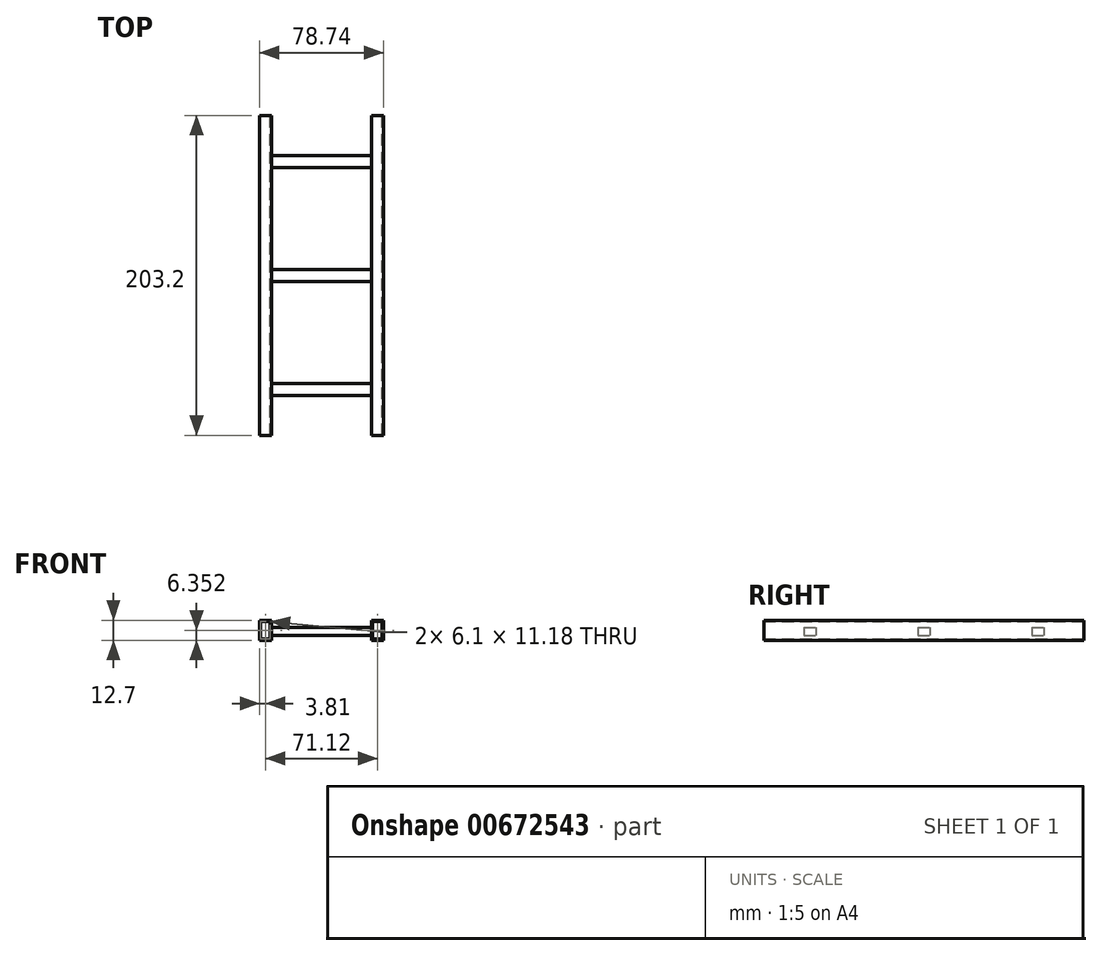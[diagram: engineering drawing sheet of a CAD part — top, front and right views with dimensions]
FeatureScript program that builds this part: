
annotation { "Feature Type Name" : "Feature", "Feature Type Description" : "" }
export const myFeature = defineFeature(function(context is Context, id is Id, definition is map)
    precondition{}
    {
        {
            var Q0;
            Q0=qCreatedBy(makeId("Front.planeOp"),FACE);
            var sketch = newSketch(context, id + "F0", { "sketchPlane" : qUnion([Q0])});
            skLineSegment(sketch, "E0.bottom", {"start": v(-39.37, 0.36) * mm, "end": v(-31.75, 0.36) * mm});
            skLineSegment(sketch, "E0.top", {"start": v(-39.37, -12.34) * mm, "end": v(-31.75, -12.34) * mm});
            skLineSegment(sketch, "E0.left", {"start": v(-39.37, 0.36) * mm, "end": v(-39.37, -12.34) * mm});
            skLineSegment(sketch, "E0.right", {"start": v(-31.75, 0.36) * mm, "end": v(-31.75, -12.34) * mm});
            skLineSegment(sketch, "E1.MirrorCS", {"start": v(31.75, 0.36) * mm, "end": v(31.75, -12.34) * mm});
            skLineSegment(sketch, "E2.MirrorCS", {"start": v(39.37, 0.36) * mm, "end": v(31.75, 0.36) * mm});
            skLineSegment(sketch, "E3.MirrorCS", {"start": v(39.37, 0.36) * mm, "end": v(39.37, -12.34) * mm});
            skLineSegment(sketch, "E4.MirrorCS", {"start": v(39.37, -12.34) * mm, "end": v(31.75, -12.34) * mm});
            skLineSegment(sketch, "E5.bottom", {"start": v(-38.6, -0.4) * mm, "end": v(-32.51, -0.4) * mm});
            skLineSegment(sketch, "E5.top", {"start": v(-38.6, -11.58) * mm, "end": v(-32.51, -11.58) * mm});
            skLineSegment(sketch, "E5.left", {"start": v(-38.6, -0.4) * mm, "end": v(-38.6, -11.58) * mm});
            skLineSegment(sketch, "E5.right", {"start": v(-32.51, -0.4) * mm, "end": v(-32.51, -11.58) * mm});
            skLineSegment(sketch, "E6.MirrorCS", {"start": v(38.6, -0.4) * mm, "end": v(32.51, -0.4) * mm});
            skLineSegment(sketch, "E7.MirrorCS", {"start": v(38.6, -0.4) * mm, "end": v(38.6, -11.58) * mm});
            skLineSegment(sketch, "E8.MirrorCS", {"start": v(38.6, -11.58) * mm, "end": v(32.51, -11.58) * mm});
            skLineSegment(sketch, "E9.MirrorCS", {"start": v(32.51, -0.4) * mm, "end": v(32.51, -11.58) * mm});
            skSolve(sketch);
        }
        {
            var Q0;
            Q0=makeQuery(id+"F0.imprint","IMPRINT",FACE,{"disambiguationData":[TD([[makeQuery(id+"F0.imprint","IMPRINT",EDGE,{"derivedFrom":sQuery(id+"F0.wireOp",EDGE,"E0.bottom")}),-1.0]])]});
            var Q1;
            Q1=makeQuery(id+"F0.imprint","IMPRINT",FACE,{"disambiguationData":[TD([[makeQuery(id+"F0.imprint","IMPRINT",EDGE,{"derivedFrom":sQuery(id+"F0.wireOp",EDGE,"E1.MirrorCS")}),1.0]])]});
            extrude(context, id + "F1", {"entities" : qUnion([Q0, Q1]), "endBound" : BoundingType.SYMMETRIC, "depth" : 203.2 * mm, "offsetDistance" : 25.4 * mm});
        }
        {
            var Q0;
            Q0=makeQuery(id+"F1.opExtrude","SWEPT_FACE",FACE,{"disambiguationData":[OSD([sQuery(id+"F0.wireOp",EDGE,"E0.right")])]});
            var sketch = newSketch(context, id + "F2", { "sketchPlane" : qUnion([Q0])});
            skLineSegment(sketch, "E10.bottom", {"start": v(-76.2, -4.28) * mm, "end": v(-68.58, -4.28) * mm});
            skLineSegment(sketch, "E10.top", {"start": v(-76.2, -9.36) * mm, "end": v(-68.58, -9.36) * mm});
            skLineSegment(sketch, "E10.left", {"start": v(-76.2, -4.28) * mm, "end": v(-76.2, -9.36) * mm});
            skLineSegment(sketch, "E10.right", {"start": v(-68.58, -4.28) * mm, "end": v(-68.58, -9.36) * mm});
            skLineSegment(sketch, "E11.bottom", {"start": v(-3.8, -4.28) * mm, "end": v(3.81, -4.28) * mm});
            skLineSegment(sketch, "E11.top", {"start": v(-3.8, -9.36) * mm, "end": v(3.81, -9.36) * mm});
            skLineSegment(sketch, "E11.left", {"start": v(-3.8, -4.28) * mm, "end": v(-3.8, -9.36) * mm});
            skLineSegment(sketch, "E11.right", {"start": v(3.81, -4.28) * mm, "end": v(3.81, -9.36) * mm});
            skLineSegment(sketch, "E12.bottom", {"start": v(68.58, -4.28) * mm, "end": v(76.2, -4.28) * mm});
            skLineSegment(sketch, "E12.top", {"start": v(68.58, -9.36) * mm, "end": v(76.2, -9.36) * mm});
            skLineSegment(sketch, "E12.left", {"start": v(68.58, -4.28) * mm, "end": v(68.58, -9.36) * mm});
            skLineSegment(sketch, "E12.right", {"start": v(76.2, -4.28) * mm, "end": v(76.2, -9.36) * mm});
            skSolve(sketch);
        }
        {
            var Q0;
            Q0=makeQuery(id+"F2.imprint","IMPRINT",FACE,{"disambiguationData":[TD([[makeQuery(id+"F2.imprint","IMPRINT",EDGE,{"derivedFrom":sQuery(id+"F2.wireOp",EDGE,"E10.bottom")}),-1.0]])]});
            var Q1;
            Q1=makeQuery(id+"F2.imprint","IMPRINT",FACE,{"disambiguationData":[TD([[makeQuery(id+"F2.imprint","IMPRINT",EDGE,{"derivedFrom":sQuery(id+"F2.wireOp",EDGE,"E11.bottom")}),-1.0]])]});
            var Q2;
            Q2=makeQuery(id+"F2.imprint","IMPRINT",FACE,{"disambiguationData":[TD([[makeQuery(id+"F2.imprint","IMPRINT",EDGE,{"derivedFrom":sQuery(id+"F2.wireOp",EDGE,"E12.bottom")}),-1.0]])]});
            extrude(context, id + "F3", {"entities" : qUnion([Q0, Q1, Q2]), "depth" : 63.5 * mm, "offsetDistance" : 25.4 * mm});
        }
    });
